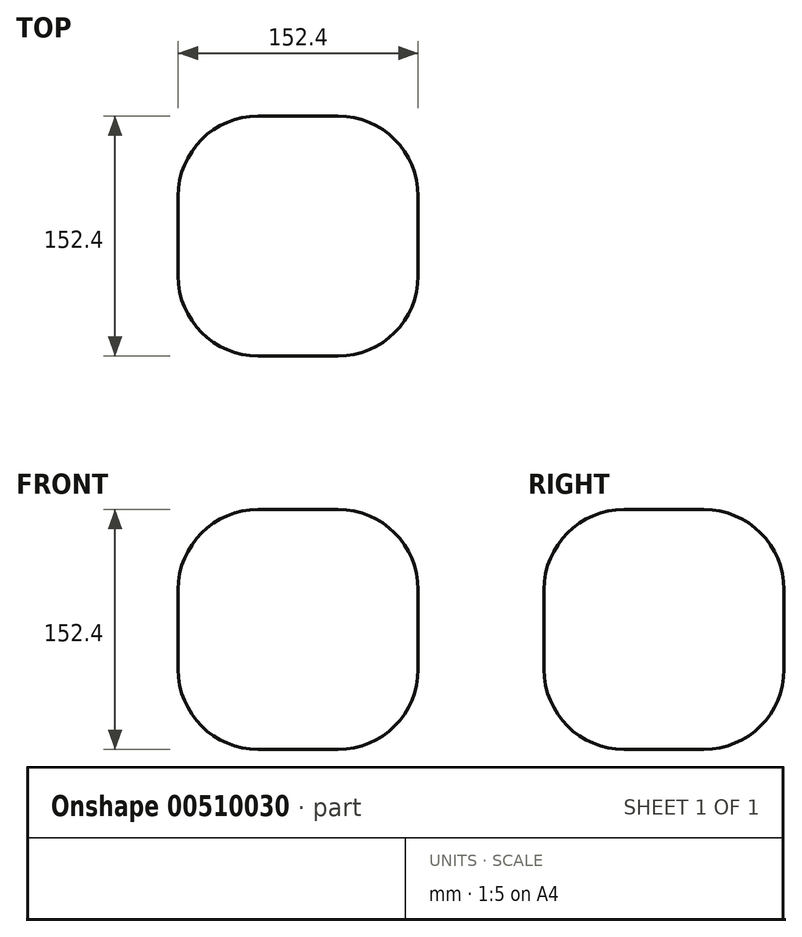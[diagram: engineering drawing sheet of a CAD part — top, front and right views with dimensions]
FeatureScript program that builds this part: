
annotation { "Feature Type Name" : "Feature", "Feature Type Description" : "" }
export const myFeature = defineFeature(function(context is Context, id is Id, definition is map)
    precondition{}
    {
        {
            var Q0;
            Q0=qCreatedBy(makeId("Top.planeOp"),FACE);
            var sketch = newSketch(context, id + "F0", { "sketchPlane" : qUnion([Q0])});
            skLineSegment(sketch, "E0.bottom", {"start": v(-76.2, 76.2) * mm, "end": v(76.2, 76.2) * mm});
            skLineSegment(sketch, "E0.top", {"start": v(-76.2, -76.2) * mm, "end": v(76.2, -76.2) * mm});
            skLineSegment(sketch, "E0.left", {"start": v(-76.2, 76.2) * mm, "end": v(-76.2, -76.2) * mm});
            skLineSegment(sketch, "E0.right", {"start": v(76.2, 76.2) * mm, "end": v(76.2, -76.2) * mm});
            skPoint(sketch, "E0.middle", {"position": v(0, 0) * mm});
            skSolve(sketch);
        }
        {
            var Q0;
            Q0=makeQuery(id+"F0.imprint","IMPRINT",FACE,{"disambiguationData":[TD([[makeQuery(id+"F0.imprint","IMPRINT",EDGE,{"derivedFrom":sQuery(id+"F0.wireOp",EDGE,"E0.bottom")}),-1.0]])]});
            extrude(context, id + "F1", {"entities" : qUnion([Q0]), "depth" : 152.4 * mm});
        }
        {
            var Q0;
            Q0=makeQuery(id+"F1.opExtrude","CAP_EDGE",EDGE,{"disambiguationData":[OSD([sQuery(id+"F0.wireOp",EDGE,"E0.top")])],"isStart":false});
            var Q1;
            Q1=makeQuery(id+"F1.opExtrude","CAP_EDGE",EDGE,{"disambiguationData":[OSD([sQuery(id+"F0.wireOp",EDGE,"E0.right")])],"isStart":false});
            var Q2;
            Q2=makeQuery(id+"F1.opExtrude","SWEPT_EDGE",EDGE,{"disambiguationData":[OSD([sQuery(id+"F0.wireOp",EDGE,"E0.top"),sQuery(id+"F0.wireOp",EDGE,"E0.right")])]});
            var Q3;
            Q3=makeQuery(id+"F1.opExtrude","SWEPT_EDGE",EDGE,{"disambiguationData":[OSD([sQuery(id+"F0.wireOp",EDGE,"E0.bottom"),sQuery(id+"F0.wireOp",EDGE,"E0.right")])]});
            var Q4;
            Q4=makeQuery(id+"F1.opExtrude","SWEPT_FACE",FACE,{"disambiguationData":[OSD([sQuery(id+"F0.wireOp",EDGE,"E0.right")])]});
            var Q5;
            Q5=makeQuery(id+"F1.opExtrude","SWEPT_FACE",FACE,{"disambiguationData":[OSD([sQuery(id+"F0.wireOp",EDGE,"E0.top")])]});
            var Q6;
            Q6=makeQuery(id+"F1.opExtrude","CAP_EDGE",EDGE,{"disambiguationData":[OSD([sQuery(id+"F0.wireOp",EDGE,"E0.left")])],"isStart":false});
            var Q7;
            Q7=makeQuery(id+"F1.opExtrude","SWEPT_FACE",FACE,{"disambiguationData":[OSD([sQuery(id+"F0.wireOp",EDGE,"E0.left")])]});
            var Q8;
            Q8=makeQuery(id+"F1.opExtrude","CAP_EDGE",EDGE,{"disambiguationData":[OSD([sQuery(id+"F0.wireOp",EDGE,"E0.bottom")])],"isStart":false});
            var Q9;
            Q9=makeQuery(id+"F1.opExtrude","SWEPT_FACE",FACE,{"disambiguationData":[OSD([sQuery(id+"F0.wireOp",EDGE,"E0.bottom")])]});
            fillet(context, id + "F2", {"entities" : qUnion([Q0, Q1, Q2, Q3, Q4, Q5, Q6, Q7, Q8, Q9]), "radius" : 50.8 * mm, "tangentPropagation" : true, "allowEdgeOverflow" : false});
        }
    });
